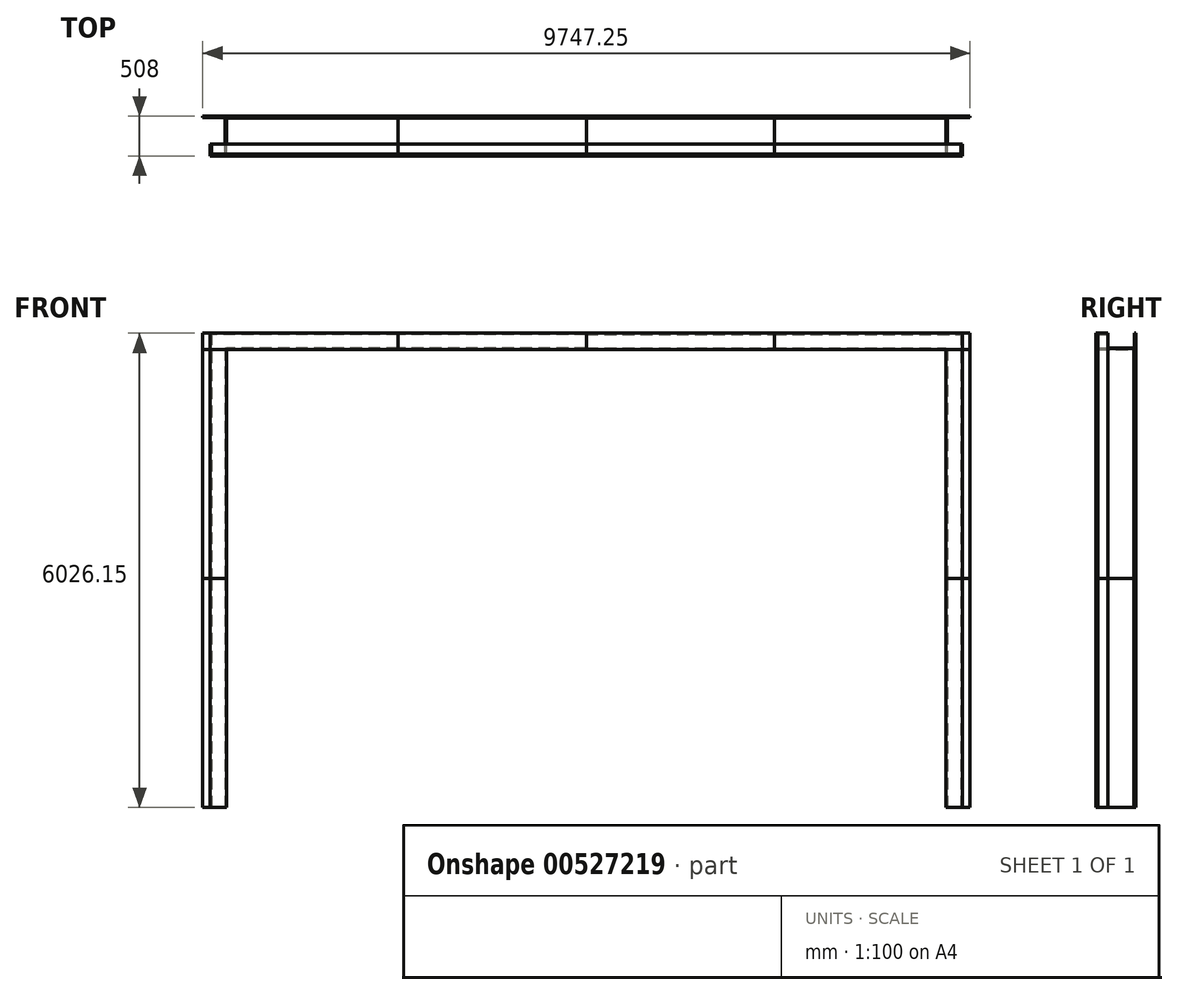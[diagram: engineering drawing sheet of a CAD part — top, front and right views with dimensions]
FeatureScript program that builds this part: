
annotation { "Feature Type Name" : "Feature", "Feature Type Description" : "" }
export const myFeature = defineFeature(function(context is Context, id is Id, definition is map)
    precondition{}
    {
        {
            var Q0;
            Q0=qCreatedBy(makeId("Top.planeOp"),FACE);
            var sketch = newSketch(context, id + "F0", { "sketchPlane" : qUnion([Q0])});
            skLineSegment(sketch, "E0.bottom", {"start": v(-114.33, -10.23) * mm, "end": v(-95.28, -10.23) * mm});
            skLineSegment(sketch, "E0.top", {"start": v(-114.33, -137.23) * mm, "end": v(-95.28, -137.23) * mm});
            skLineSegment(sketch, "E0.left", {"start": v(-114.33, -10.23) * mm, "end": v(-114.33, -137.23) * mm});
            skLineSegment(sketch, "E0.right", {"start": v(-95.28, -10.23) * mm, "end": v(-95.28, -137.23) * mm});
            skLineSegment(sketch, "E1.bottom", {"start": v(-114.33, -143.58) * mm, "end": v(95.22, -143.58) * mm});
            skLineSegment(sketch, "E1.top", {"start": v(-114.33, -162.63) * mm, "end": v(95.22, -162.63) * mm});
            skLineSegment(sketch, "E1.left", {"start": v(-114.33, -143.58) * mm, "end": v(-114.33, -162.63) * mm});
            skLineSegment(sketch, "E1.right", {"start": v(95.22, -143.58) * mm, "end": v(95.22, -162.63) * mm});
            skLineSegment(sketch, "E2.bottom", {"start": v(95.22, -137.23) * mm, "end": v(76.17, -137.23) * mm});
            skLineSegment(sketch, "E2.left", {"start": v(95.22, -137.23) * mm, "end": v(95.22, 319.97) * mm});
            skLineSegment(sketch, "E2.right", {"start": v(76.17, -137.23) * mm, "end": v(76.17, 319.97) * mm});
            skLineSegment(sketch, "E3.bottom", {"start": v(95.22, 345.37) * mm, "end": v(-209.58, 345.37) * mm});
            skLineSegment(sketch, "E3.top", {"start": v(95.22, 326.32) * mm, "end": v(-209.58, 326.32) * mm});
            skLineSegment(sketch, "E3.left", {"start": v(95.22, 345.37) * mm, "end": v(95.22, 326.32) * mm});
            skLineSegment(sketch, "E3.right", {"start": v(-209.58, 345.37) * mm, "end": v(-209.58, 326.32) * mm});
            skLineSegment(sketch, "E4", {"start": v(76.17, 319.97) * mm, "end": v(95.22, 319.97) * mm});
            skSolve(sketch);
        }
        {
            var Q0;
            Q0 = qSketchRegion(id + "F0", true);
            extrude(context, id + "F1", {"entities" : qUnion([Q0]), "depth" : 2908.3 * mm, "offsetDistance" : 25.4 * mm});
        }
        {
            var Q0;
            Q0=makeQuery(id+"F1.opExtrude","CAP_FACE",FACE,{"disambiguationData":[OSD([sQuery(id+"F0.wireOp",EDGE,"E1.bottom"),sQuery(id+"F0.wireOp",EDGE,"E1.top"),sQuery(id+"F0.wireOp",EDGE,"E1.left"),sQuery(id+"F0.wireOp",EDGE,"E1.right")])],"isStart":false});
            var sketch = newSketch(context, id + "F2", { "sketchPlane" : qUnion([Q0])});
            skLineSegment(sketch, "E5.bottom", {"start": v(-114.33, -143.58) * mm, "end": v(95.22, -143.58) * mm});
            skLineSegment(sketch, "E5.top", {"start": v(-114.33, -162.63) * mm, "end": v(95.22, -162.63) * mm});
            skLineSegment(sketch, "E5.left", {"start": v(-114.33, -143.58) * mm, "end": v(-114.33, -162.63) * mm});
            skLineSegment(sketch, "E5.right", {"start": v(95.22, -143.58) * mm, "end": v(95.22, -162.63) * mm});
            skLineSegment(sketch, "E6.0.0", {"start": v(-209.58, 326.32) * mm, "end": v(95.22, 326.32) * mm});
            skLineSegment(sketch, "E6.0.1", {"start": v(95.22, 326.32) * mm, "end": v(95.22, 345.37) * mm});
            skLineSegment(sketch, "E6.0.2", {"start": v(95.22, 345.37) * mm, "end": v(-209.58, 345.37) * mm});
            skLineSegment(sketch, "E6.0.3", {"start": v(-209.58, 345.37) * mm, "end": v(-209.58, 326.32) * mm});
            skSolve(sketch);
        }
        {
            var Q0;
            Q0 = qSketchRegion(id + "F2", true);
            extrude(context, id + "F3", {"entities" : qUnion([Q0]), "depth" : 2908.3 * mm, "offsetDistance" : 25.4 * mm});
        }
        {
            var Q0;
            Q0=makeQuery(id+"F1.opExtrude","CAP_FACE",FACE,{"disambiguationData":[OSD([sQuery(id+"F0.wireOp",EDGE,"E0.bottom"),sQuery(id+"F0.wireOp",EDGE,"E0.top"),sQuery(id+"F0.wireOp",EDGE,"E0.left"),sQuery(id+"F0.wireOp",EDGE,"E0.right")])],"isStart":false});
            var sketch = newSketch(context, id + "F4", { "sketchPlane" : qUnion([Q0])});
            skLineSegment(sketch, "E7.0.0", {"start": v(-114.33, -10.23) * mm, "end": v(-114.33, -137.23) * mm});
            skLineSegment(sketch, "E7.0.1", {"start": v(-114.33, -137.23) * mm, "end": v(-95.28, -137.23) * mm});
            skLineSegment(sketch, "E7.0.2", {"start": v(-95.28, -137.23) * mm, "end": v(-95.28, -10.23) * mm});
            skLineSegment(sketch, "E7.0.3", {"start": v(-95.28, -10.23) * mm, "end": v(-114.33, -10.23) * mm});
            skSolve(sketch);
        }
        {
            var Q0;
            Q0 = qSketchRegion(id + "F4", true);
            extrude(context, id + "F5", {"entities" : qUnion([Q0]), "depth" : 3117.85 * mm, "offsetDistance" : 25.4 * mm});
        }
        {
            var Q0;
            Q0=makeQuery(id+"F1.opExtrude","CAP_FACE",FACE,{"disambiguationData":[OSD([sQuery(id+"F0.wireOp",EDGE,"E2.bottom"),sQuery(id+"F0.wireOp",EDGE,"E2.top"),sQuery(id+"F0.wireOp",EDGE,"E2.left"),sQuery(id+"F0.wireOp",EDGE,"E2.right")])],"isStart":false});
            var sketch = newSketch(context, id + "F6", { "sketchPlane" : qUnion([Q0])});
            skLineSegment(sketch, "E8.0.0", {"start": v(95.22, 319.97) * mm, "end": v(76.17, 319.97) * mm});
            skLineSegment(sketch, "E8.0.1", {"start": v(76.17, 319.97) * mm, "end": v(76.17, -137.23) * mm});
            skLineSegment(sketch, "E8.0.2", {"start": v(76.17, -137.23) * mm, "end": v(95.22, -137.23) * mm});
            skLineSegment(sketch, "E8.0.3", {"start": v(95.22, -137.23) * mm, "end": v(95.22, 319.97) * mm});
            skSolve(sketch);
        }
        {
            var Q0;
            Q0 = qSketchRegion(id + "F6", true);
            extrude(context, id + "F7", {"entities" : qUnion([Q0]), "depth" : 2921 * mm, "offsetDistance" : 25.4 * mm});
        }
        {
            var Q0;
            Q0=makeQuery(id+"F5.opExtrude","SWEPT_FACE",FACE,{"disambiguationData":[OSD([sQuery(id+"F4.wireOp",EDGE,"E7.0.0")])]});
            cPlane(context, id + "F8", {"entities" : qUnion([Q0]), "cplaneType" : CPlaneType.OFFSET, "offset" : 2389.2 * mm, "oppositeDirection" : true, "width" : 152.4 * mm, "height" : 152.4 * mm});
        }
        {
            var Q0;
            Q0=makeQuery(id+"F5.opExtrude","SWEPT_FACE",FACE,{"disambiguationData":[OSD([sQuery(id+"F4.wireOp",EDGE,"E7.0.2")])]});
            var sketch = newSketch(context, id + "F9", { "sketchPlane" : qUnion([Q0])});
            skLineSegment(sketch, "E9.bottom", {"start": v(-137.23, 6026.15) * mm, "end": v(-10.23, 6026.15) * mm});
            skLineSegment(sketch, "E9.top", {"start": v(-137.23, 6007.1) * mm, "end": v(-10.23, 6007.1) * mm});
            skLineSegment(sketch, "E9.left", {"start": v(-137.23, 6026.15) * mm, "end": v(-137.23, 6007.1) * mm});
            skLineSegment(sketch, "E9.right", {"start": v(-10.23, 6026.15) * mm, "end": v(-10.23, 6007.1) * mm});
            skSolve(sketch);
        }
        {
            var Q0;
            Q0 = qSketchRegion(id + "F9", true);
            var Q1;
            Q1=qCreatedBy(id+"F8.planeOp",FACE);
            extrude(context, id + "F10", {"entities" : qUnion([Q0]), "endBound" : BoundingType.UP_TO_SURFACE, "depth" : 25.4 * mm, "endBoundEntityFace" : qUnion([Q1]), "offsetDistance" : 25.4 * mm});
        }
        {
            var Q0;
            Q0=makeQuery(id+"F3.opExtrude","SWEPT_FACE",FACE,{"disambiguationData":[OSD([sQuery(id+"F2.wireOp",EDGE,"E5.top")])]});
            var sketch = newSketch(context, id + "F11", { "sketchPlane" : qUnion([Q0])});
            skLineSegment(sketch, "E10.bottom", {"start": v(-114.33, 5816.6) * mm, "end": v(2274.85, 5816.6) * mm});
            skLineSegment(sketch, "E10.top", {"start": v(-114.33, 6026.15) * mm, "end": v(2274.85, 6026.15) * mm});
            skLineSegment(sketch, "E10.left", {"start": v(-114.33, 5816.6) * mm, "end": v(-114.33, 6026.15) * mm});
            skLineSegment(sketch, "E10.right", {"start": v(2274.85, 5816.6) * mm, "end": v(2274.85, 6026.15) * mm});
            skSolve(sketch);
        }
        {
            var Q0;
            Q0 = qSketchRegion(id + "F11", true);
            extrude(context, id + "F12", {"entities" : qUnion([Q0]), "oppositeDirection" : true, "depth" : 19.05 * mm, "offsetDistance" : 25.4 * mm});
        }
        {
            var Q0;
            Q0=makeQuery(id+"F7.opExtrude","SWEPT_FACE",FACE,{"disambiguationData":[OSD([sQuery(id+"F6.wireOp",EDGE,"E8.0.3")])]});
            var sketch = newSketch(context, id + "F13", { "sketchPlane" : qUnion([Q0])});
            skLineSegment(sketch, "E11.bottom", {"start": v(-137.23, 5816.6) * mm, "end": v(319.97, 5816.6) * mm});
            skLineSegment(sketch, "E11.top", {"start": v(-137.23, 5835.65) * mm, "end": v(319.97, 5835.65) * mm});
            skLineSegment(sketch, "E11.left", {"start": v(-137.23, 5816.6) * mm, "end": v(-137.23, 5835.65) * mm});
            skLineSegment(sketch, "E11.right", {"start": v(319.97, 5816.6) * mm, "end": v(319.97, 5835.65) * mm});
            skSolve(sketch);
        }
        {
            var Q0;
            Q0 = qSketchRegion(id + "F13", true);
            var Q1;
            Q1=qCreatedBy(id+"F8.planeOp",FACE);
            extrude(context, id + "F14", {"entities" : qUnion([Q0]), "endBound" : BoundingType.UP_TO_SURFACE, "depth" : 25.4 * mm, "endBoundEntityFace" : qUnion([Q1]), "offsetDistance" : 25.4 * mm});
        }
        {
            var Q0;
            Q0=makeQuery(id+"F3.opExtrude","SWEPT_FACE",FACE,{"disambiguationData":[OSD([sQuery(id+"F2.wireOp",EDGE,"E6.0.2")])]});
            var sketch = newSketch(context, id + "F15", { "sketchPlane" : qUnion([Q0])});
            skLineSegment(sketch, "E12.bottom", {"start": v(209.58, 5816.6) * mm, "end": v(-2274.85, 5816.6) * mm});
            skLineSegment(sketch, "E12.top", {"start": v(209.58, 6026.15) * mm, "end": v(-2274.85, 6026.15) * mm});
            skLineSegment(sketch, "E12.left", {"start": v(209.58, 5816.6) * mm, "end": v(209.58, 6026.15) * mm});
            skLineSegment(sketch, "E12.right", {"start": v(-2274.85, 5816.6) * mm, "end": v(-2274.85, 6026.15) * mm});
            skSolve(sketch);
        }
        {
            var Q0;
            Q0 = qSketchRegion(id + "F15", true);
            extrude(context, id + "F16", {"entities" : qUnion([Q0]), "oppositeDirection" : true, "depth" : 19.05 * mm, "offsetDistance" : 25.4 * mm});
        }
        {
            var Q0;
            Q0=makeQuery(id+"F12.opExtrude","SWEPT_FACE",FACE,{"disambiguationData":[OSD([sQuery(id+"F11.wireOp",EDGE,"E10.right")])]});
            var sketch = newSketch(context, id + "F17", { "sketchPlane" : qUnion([Q0])});
            skLineSegment(sketch, "E13.0.0", {"start": v(-137.23, 6007.1) * mm, "end": v(-10.23, 6007.1) * mm});
            skLineSegment(sketch, "E13.0.1", {"start": v(-10.23, 6007.1) * mm, "end": v(-10.23, 6026.15) * mm});
            skLineSegment(sketch, "E13.0.2", {"start": v(-10.23, 6026.15) * mm, "end": v(-137.23, 6026.15) * mm});
            skLineSegment(sketch, "E13.0.3", {"start": v(-137.23, 6026.15) * mm, "end": v(-137.23, 6007.1) * mm});
            skLineSegment(sketch, "E14.0.0", {"start": v(-137.23, 5835.65) * mm, "end": v(-137.23, 5816.6) * mm});
            skLineSegment(sketch, "E14.0.1", {"start": v(-137.23, 5816.6) * mm, "end": v(319.97, 5816.6) * mm});
            skLineSegment(sketch, "E14.0.2", {"start": v(319.97, 5816.6) * mm, "end": v(319.97, 5835.65) * mm});
            skLineSegment(sketch, "E14.0.3", {"start": v(319.97, 5835.65) * mm, "end": v(-137.23, 5835.65) * mm});
            skLineSegment(sketch, "E15.0.0", {"start": v(345.37, 5816.6) * mm, "end": v(345.37, 6026.15) * mm});
            skLineSegment(sketch, "E15.0.1", {"start": v(345.37, 6026.15) * mm, "end": v(326.32, 6026.15) * mm});
            skLineSegment(sketch, "E15.0.2", {"start": v(326.32, 6026.15) * mm, "end": v(326.32, 5816.6) * mm});
            skLineSegment(sketch, "E15.0.3", {"start": v(326.32, 5816.6) * mm, "end": v(345.37, 5816.6) * mm});
            skLineSegment(sketch, "E16.bottom", {"start": v(-162.63, 6026.15) * mm, "end": v(-143.58, 6026.15) * mm});
            skLineSegment(sketch, "E16.top", {"start": v(-162.63, 5816.6) * mm, "end": v(-143.58, 5816.6) * mm});
            skLineSegment(sketch, "E16.left", {"start": v(-162.63, 6026.15) * mm, "end": v(-162.63, 5816.6) * mm});
            skLineSegment(sketch, "E16.right", {"start": v(-143.58, 6026.15) * mm, "end": v(-143.58, 5816.6) * mm});
            skSolve(sketch);
        }
        {
            var Q0;
            Q0 = qSketchRegion(id + "F17", true);
            extrude(context, id + "F18", {"entities" : qUnion([Q0]), "depth" : 2389.2 * mm, "offsetDistance" : 25.4 * mm});
        }
        {
            var Q0;
            Q0=makeQuery(id+"F10.opExtrude","SWEPT_BODY",BODY,{"disambiguationData":[OSD([sQuery(id+"F9.wireOp",EDGE,"E9.bottom"),sQuery(id+"F9.wireOp",EDGE,"E9.top"),sQuery(id+"F9.wireOp",EDGE,"E9.left"),sQuery(id+"F9.wireOp",EDGE,"E9.right")])]});
            var Q1;
            Q1=makeQuery(id+"F14.opExtrude","SWEPT_BODY",BODY,{"disambiguationData":[OSD([sQuery(id+"F13.wireOp",EDGE,"E11.bottom"),sQuery(id+"F13.wireOp",EDGE,"E11.top"),sQuery(id+"F13.wireOp",EDGE,"E11.left"),sQuery(id+"F13.wireOp",EDGE,"E11.right")])]});
            var Q2;
            Q2=makeQuery(id+"F3.opExtrude","SWEPT_BODY",BODY,{"disambiguationData":[OSD([sQuery(id+"F2.wireOp",EDGE,"E6.0.0"),sQuery(id+"F2.wireOp",EDGE,"E6.0.1"),sQuery(id+"F2.wireOp",EDGE,"E6.0.2"),sQuery(id+"F2.wireOp",EDGE,"E6.0.3")])]});
            var Q3;
            Q3=makeQuery(id+"F16.opExtrude","SWEPT_BODY",BODY,{"disambiguationData":[OSD([sQuery(id+"F15.wireOp",EDGE,"E12.bottom"),sQuery(id+"F15.wireOp",EDGE,"E12.top"),sQuery(id+"F15.wireOp",EDGE,"E12.left"),sQuery(id+"F15.wireOp",EDGE,"E12.right")])]});
            var Q4;
            Q4=makeQuery(id+"F12.opExtrude","SWEPT_BODY",BODY,{"disambiguationData":[OSD([sQuery(id+"F11.wireOp",EDGE,"E10.bottom"),sQuery(id+"F11.wireOp",EDGE,"E10.top"),sQuery(id+"F11.wireOp",EDGE,"E10.left"),sQuery(id+"F11.wireOp",EDGE,"E10.right")])]});
            var Q5;
            Q5=makeQuery(id+"F5.opExtrude","SWEPT_BODY",BODY,{"disambiguationData":[OSD([sQuery(id+"F4.wireOp",EDGE,"E7.0.0"),sQuery(id+"F4.wireOp",EDGE,"E7.0.1"),sQuery(id+"F4.wireOp",EDGE,"E7.0.2"),sQuery(id+"F4.wireOp",EDGE,"E7.0.3")])]});
            var Q6;
            Q6=makeQuery(id+"F1.opExtrude","SWEPT_BODY",BODY,{"disambiguationData":[OSD([sQuery(id+"F0.wireOp",EDGE,"E3.bottom"),sQuery(id+"F0.wireOp",EDGE,"E3.top"),sQuery(id+"F0.wireOp",EDGE,"E3.left"),sQuery(id+"F0.wireOp",EDGE,"E3.right")])]});
            var Q7;
            Q7=makeQuery(id+"F7.opExtrude","SWEPT_BODY",BODY,{"disambiguationData":[OSD([sQuery(id+"F6.wireOp",EDGE,"E8.0.0"),sQuery(id+"F6.wireOp",EDGE,"E8.0.1"),sQuery(id+"F6.wireOp",EDGE,"E8.0.2"),sQuery(id+"F6.wireOp",EDGE,"E8.0.3")])]});
            var Q8;
            Q8=makeQuery(id+"F1.opExtrude","SWEPT_BODY",BODY,{"disambiguationData":[OSD([sQuery(id+"F0.wireOp",EDGE,"E2.bottom"),sQuery(id+"F0.wireOp",EDGE,"E2.left"),sQuery(id+"F0.wireOp",EDGE,"E2.right"),sQuery(id+"F0.wireOp",EDGE,"E4")])]});
            var Q9;
            Q9=makeQuery(id+"F1.opExtrude","SWEPT_BODY",BODY,{"disambiguationData":[OSD([sQuery(id+"F0.wireOp",EDGE,"E1.bottom"),sQuery(id+"F0.wireOp",EDGE,"E1.top"),sQuery(id+"F0.wireOp",EDGE,"E1.left"),sQuery(id+"F0.wireOp",EDGE,"E1.right")])]});
            var Q10;
            Q10=makeQuery(id+"F3.opExtrude","SWEPT_BODY",BODY,{"disambiguationData":[OSD([sQuery(id+"F2.wireOp",EDGE,"E5.bottom"),sQuery(id+"F2.wireOp",EDGE,"E5.top"),sQuery(id+"F2.wireOp",EDGE,"E5.left"),sQuery(id+"F2.wireOp",EDGE,"E5.right")])]});
            var Q11;
            Q11=makeQuery(id+"F1.opExtrude","SWEPT_BODY",BODY,{"disambiguationData":[OSD([sQuery(id+"F0.wireOp",EDGE,"E0.bottom"),sQuery(id+"F0.wireOp",EDGE,"E0.top"),sQuery(id+"F0.wireOp",EDGE,"E0.left"),sQuery(id+"F0.wireOp",EDGE,"E0.right")])]});
            var Q12;
            Q12=makeQuery(id+"F18.opExtrude","SWEPT_BODY",BODY,{"disambiguationData":[OSD([sQuery(id+"F17.wireOp",EDGE,"E16.bottom"),sQuery(id+"F17.wireOp",EDGE,"E16.top"),sQuery(id+"F17.wireOp",EDGE,"E16.left"),sQuery(id+"F17.wireOp",EDGE,"E16.right")])]});
            var Q13;
            Q13=makeQuery(id+"F18.opExtrude","SWEPT_BODY",BODY,{"disambiguationData":[OSD([sQuery(id+"F17.wireOp",EDGE,"E15.0.0"),sQuery(id+"F17.wireOp",EDGE,"E15.0.1"),sQuery(id+"F17.wireOp",EDGE,"E15.0.2"),sQuery(id+"F17.wireOp",EDGE,"E15.0.3")])]});
            var Q14;
            Q14=makeQuery(id+"F18.opExtrude","SWEPT_BODY",BODY,{"disambiguationData":[OSD([sQuery(id+"F17.wireOp",EDGE,"E14.0.0"),sQuery(id+"F17.wireOp",EDGE,"E14.0.1"),sQuery(id+"F17.wireOp",EDGE,"E14.0.2"),sQuery(id+"F17.wireOp",EDGE,"E14.0.3")])]});
            var Q15;
            Q15=makeQuery(id+"F18.opExtrude","SWEPT_BODY",BODY,{"disambiguationData":[OSD([sQuery(id+"F17.wireOp",EDGE,"E13.0.0"),sQuery(id+"F17.wireOp",EDGE,"E13.0.1"),sQuery(id+"F17.wireOp",EDGE,"E13.0.2"),sQuery(id+"F17.wireOp",EDGE,"E13.0.3")])]});
            var Q16;
            Q16=makeQuery(id+"F18.opExtrude","CAP_FACE",FACE,{"disambiguationData":[OSD([sQuery(id+"F17.wireOp",EDGE,"E16.bottom"),sQuery(id+"F17.wireOp",EDGE,"E16.top"),sQuery(id+"F17.wireOp",EDGE,"E16.left"),sQuery(id+"F17.wireOp",EDGE,"E16.right")])],"isStart":false});
            mirror(context, id + "F19", {"entities" : qUnion([Q0, Q1, Q2, Q3, Q4, Q5, Q6, Q7, Q8, Q9, Q10, Q11, Q12, Q13, Q14, Q15]), "mirrorPlane" : qUnion([Q16])});
        }
    });
